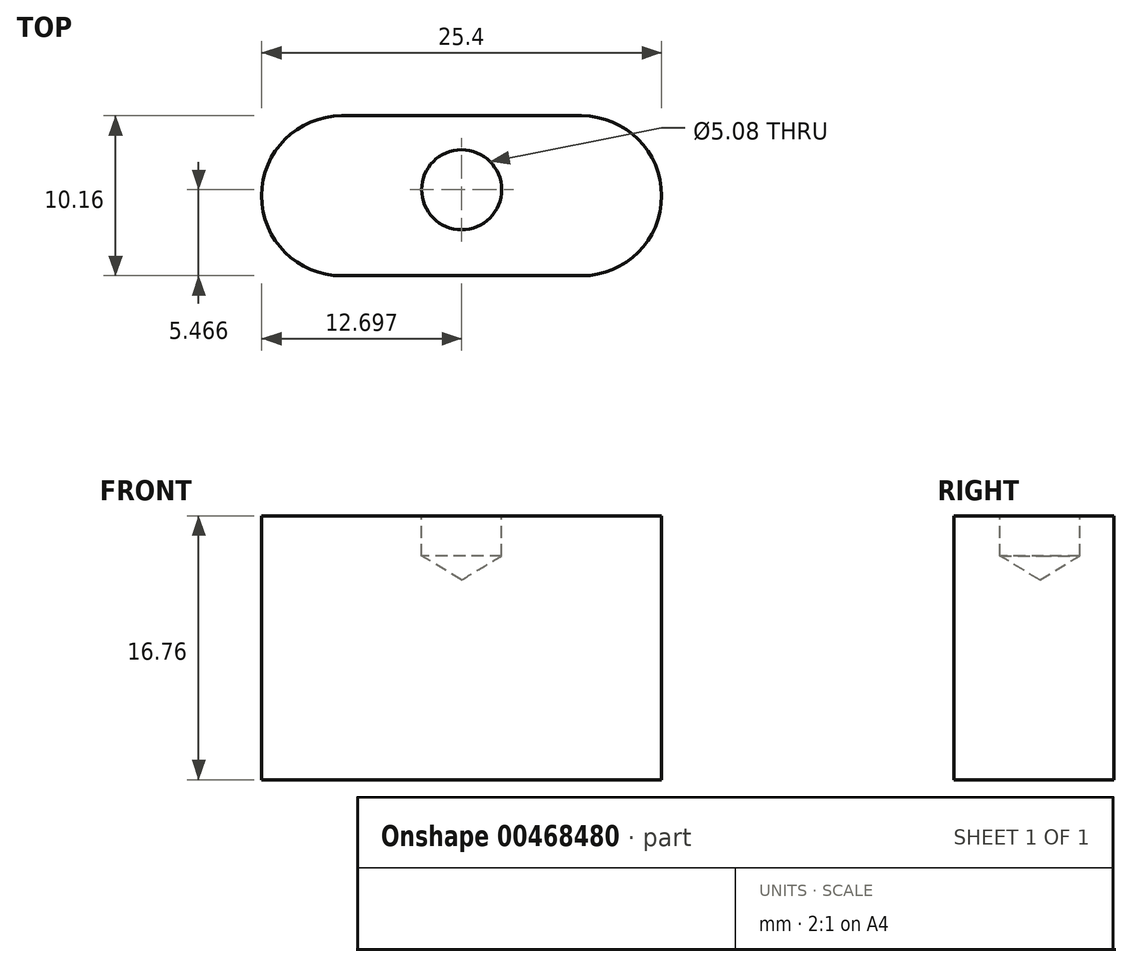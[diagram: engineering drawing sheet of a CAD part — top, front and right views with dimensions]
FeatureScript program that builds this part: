
annotation { "Feature Type Name" : "Feature", "Feature Type Description" : "" }
export const myFeature = defineFeature(function(context is Context, id is Id, definition is map)
    precondition{}
    {
        {
            var Q0;
            Q0=qCreatedBy(makeId("Top.planeOp"),FACE);
            var sketch = newSketch(context, id + "F0", { "sketchPlane" : qUnion([Q0])});
            skLineSegment(sketch, "E0.bottom", {"start": v(-21.04, 0) * mm, "end": v(-5.8, 0) * mm});
            skLineSegment(sketch, "E0.top", {"start": v(-21.04, -10.16) * mm, "end": v(-5.8, -10.16) * mm});
            skLineSegment(sketch, "E0.left", {"start": v(-26.12, -5.08) * mm, "end": v(-26.12, -5.08) * mm});
            skLineSegment(sketch, "E0.right", {"start": v(-0.72, -5.08) * mm, "end": v(-0.72, -5.08) * mm});
            skPoint(sketch, "E1.visualSharp", {"position": v(-26.12, 0) * mm});
            skArc(sketch, "E1.filletArc", {"start": v(-21.04, 0) * mm, "mid": v(-24.64, -1.49) * mm, "end": v(-26.12, -5.08) * mm});
            skPoint(sketch, "E2.visualSharp", {"position": v(-0.72, 0) * mm});
            skArc(sketch, "E2.filletArc", {"start": v(-0.72, -5.08) * mm, "mid": v(-2.21, -1.49) * mm, "end": v(-5.8, 0) * mm});
            skPoint(sketch, "E3.visualSharp", {"position": v(-0.72, -10.16) * mm});
            skArc(sketch, "E3.filletArc", {"start": v(-5.8, -10.16) * mm, "mid": v(-2.21, -8.67) * mm, "end": v(-0.72, -5.08) * mm});
            skPoint(sketch, "E4.visualSharp", {"position": v(-26.12, -10.16) * mm});
            skArc(sketch, "E4.filletArc", {"start": v(-26.12, -5.08) * mm, "mid": v(-24.64, -8.67) * mm, "end": v(-21.04, -10.16) * mm});
            skPoint(sketch, "E5", {"position": v(-13.42, -4.7) * mm});
            skPoint(sketch, "E5.positionSnap0", {"position": v(-13.42, -10.16) * mm});
            skSolve(sketch);
        }
        {
            var Q0;
            Q0 = qSketchRegion(id + "F0", true);
            extrude(context, id + "F1", {"entities" : qUnion([Q0]), "oppositeDirection" : true, "depth" : 16.76 * mm});
        }
        {
            var Q0;
            Q0=sQuery(id+"F0.wireOp",VERTEX,"E5");
            var Q1;
            Q1=makeQuery(id+"F1.opExtrude","SWEPT_BODY",BODY,{"disambiguationData":[OSD([sQuery(id+"F0.wireOp",EDGE,"E0.bottom"),sQuery(id+"F0.wireOp",EDGE,"E0.top"),sQuery(id+"F0.wireOp",EDGE,"E1.filletArc"),sQuery(id+"F0.wireOp",EDGE,"E2.filletArc"),sQuery(id+"F0.wireOp",EDGE,"E3.filletArc"),sQuery(id+"F0.wireOp",EDGE,"E4.filletArc")])]});
            hole(context, id + "F2", {"style" : HoleStyle.SIMPLE, "endStyle" : HoleEndStyle.BLIND, "holeDiameter" : 5.08 * mm, "holeDepth" : 2.54 * mm, "isTappedThrough" : true, "tappedDepth" : 12.7 * mm, "tapClearance" : 3, "locations" : qUnion([Q0]), "scope" : qUnion([Q1])});
        }
    });
